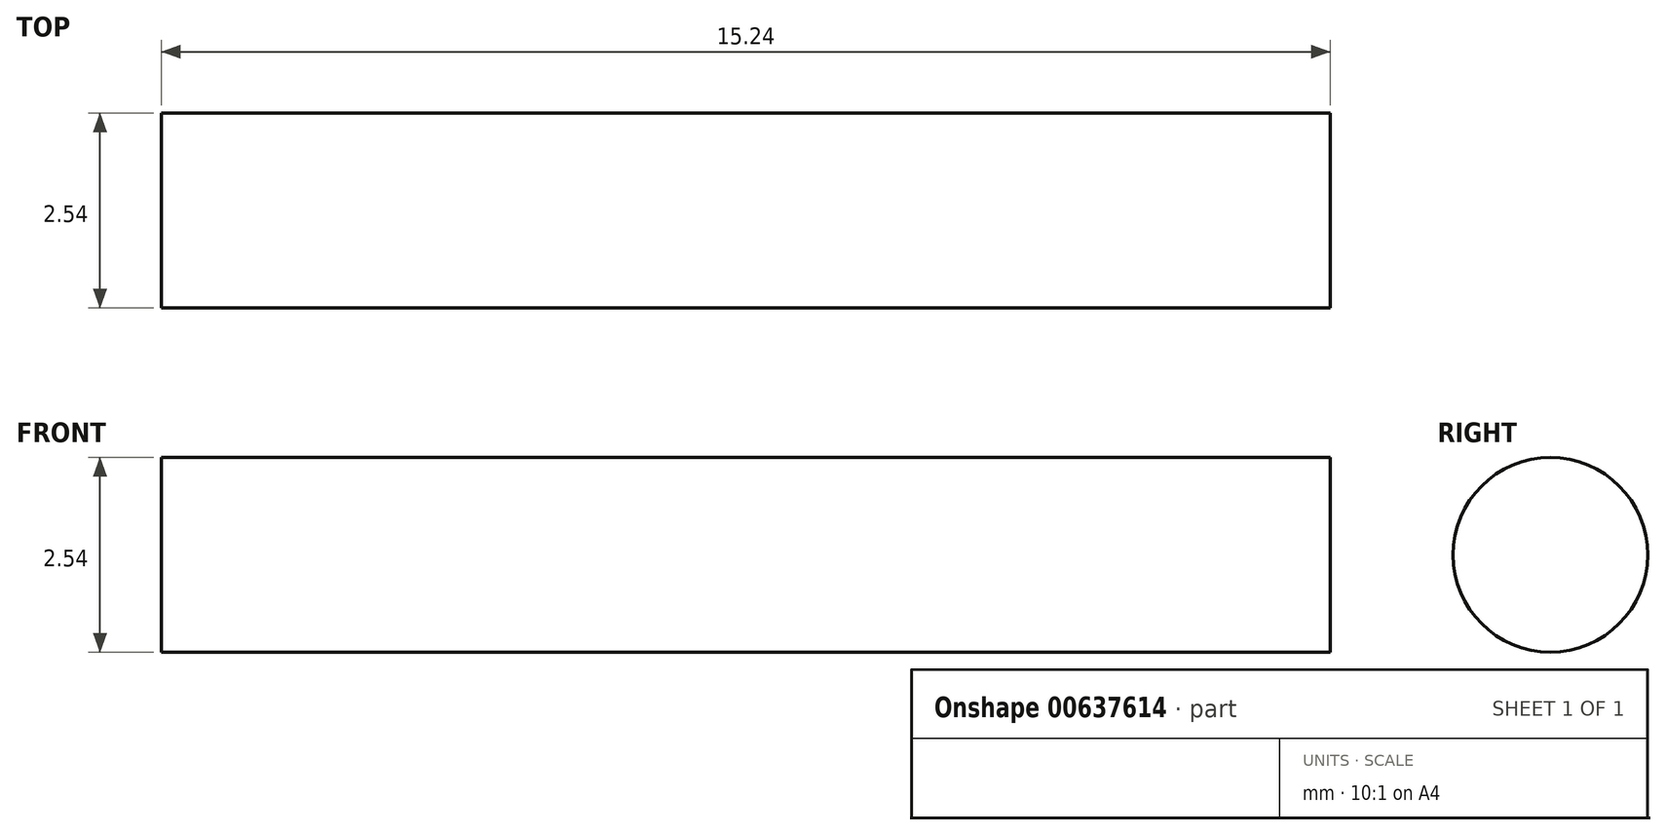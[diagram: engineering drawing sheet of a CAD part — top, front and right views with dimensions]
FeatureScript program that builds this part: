
annotation { "Feature Type Name" : "Feature", "Feature Type Description" : "" }
export const myFeature = defineFeature(function(context is Context, id is Id, definition is map)
    precondition{}
    {
        {
            var Q0;
            Q0=qCreatedBy(makeId("Right.planeOp"),FACE);
            var sketch = newSketch(context, id + "F0", { "sketchPlane" : qUnion([Q0])});
            skCircle(sketch, "E0", {"center": v(0, 0) * mm, "radius": 1.27 * mm});
            skSolve(sketch);
        }
        {
            var Q0;
            Q0=qSketchRegion(id+"F0",true);
            extrude(context, id + "F1", {"entities" : qUnion([Q0]), "depth" : 15.24 * mm});
        }
    });
